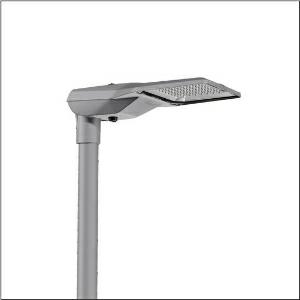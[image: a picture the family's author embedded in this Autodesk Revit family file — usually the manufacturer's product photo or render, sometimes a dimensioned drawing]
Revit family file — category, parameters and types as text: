
# Revit family: streetlight_sl_21_midi___p0_8ab_5xe3r33t08nb_adf9
name_source: partatom
category: Lighting Fixtures
units: mm (PartAtom-declared; Revit-internal decimal feet)

## family parameters
Cut with Voids When Loaded = No
Host = Face
Light Source = No
Part Type = Normal
Room Calculation Point = No
Round Connector Dimension = Use Diameter
Shared = No

## types (1)
- --- (1 x LED, 19710 lm, 151.2 W, 3000K)
    Apparent Load = 151 VA
    CIE Flux Codes = 39 72 97 100 100
    Color Rendering = 70
    Color Temperature = 3000K
    Default Elevation = 1800 mm
    Description = Streetlight SL 21 midi, mast luminaire, primary light control with lens, of PMMA, primary optical cover: cover, of toughened safety glass, transparent, light distribution: P0.8aB, light emission: direct distribution, primary light characteristic: asymmetric, installation type: post-top, side-entry, LED, High Power LED, rated luminous flux: 19.710lm, luminous efficacy: 130lm/W, light colour: 730, colour temperature: 3000K, control gear: D4i, control: pre-setting: logarithmic dimming characteristic, flexible luminous flux parameterisation, time-dependent luminous flux control, constant luminous flux control, overheat protection, mains connection: 230..240V, AC, 50/60Hz, start of lifetime: 151W, end of service life: 157W, reduction: 70W, luminaire housing, of diecast aluminium, powder-coated, Siteco® metallic grey (DB 702S), corrosivity category C5 mid according to DIN EN ISO 12944, multi-level sealing system, sealing non-destructively replaceable, inclination adjustable: 0°, 5°, 10°, 15°, please order mast flange separately, length: 644mm, width: 335mm, height: 110mm, mast flange for spigot size: 42mm (side-entry): 5XC10008XM4, 60/48mm (side-entry/post-top): 5XC10108XM2, 76/60mm (side-entry/post-top): 5XC10108XM1, mounting height: 4..8m, Smart Interface below and above, protection rating (complete): IP66, insulation class (complete): insulation class II (safety insulation), certification: CE, ENEC, ENEC+, VDE, impact resistance: IK09, permissible operating ambient temperature for outdoor applications: -40..+50°C, standard-compliant lighting for roads and squares, packaging unit: 1 piece

Light Distribution: P0.8aB
    Height = 111 mm
    Lamp = 1 x LED
    Lamp Light Flux = 19710 lm
    Lamp Power = 151.2 W
    Lamp count = 1
    Length = 644 mm
    Luminous efficacy = 130 lm/W
    Manufacturer = Siteco
    ModVariant = No
    Model = 5XE3R33T08NB
    Number of Poles = 1
    OnlyDefault = Yes
    Power Factor = 1
    Product Name = Streetlight SL 21 midi | P0.8aB
    Product group = mast luminaire | pylon top
    ProductGroupID = 6100
    Protection Class = Protection class II
    Protection Degree = IP 66
    RLX_Detail_Level = 1
    RLX_Emergency_Light_Flux = 0 lm
    RLX_Emergency_Type = 0
    RLX_Emergency_Type_DB = No
    RlxData = <blob elided: 90897 chars, md5=10f8d2f3>
    Socket = socket
    Standby Power = 0 W
    System Light Flux = 19710 lm
    System Power = 151 W
    Type Comments = factory setting: luminous flux: 100 % | dim-lin: 254 | 802 mA
    Type Image = l_1004304.jpg
    URL = http://relux.com
    VarID = @adj_067834
    Voltage = 0 V
    Weight = 0.00 kg
    Width = 336 mm

## geometry (parser evidence)
native form markers: Blend x4, Sweep x11
no freeform markers — native parametric forms only
